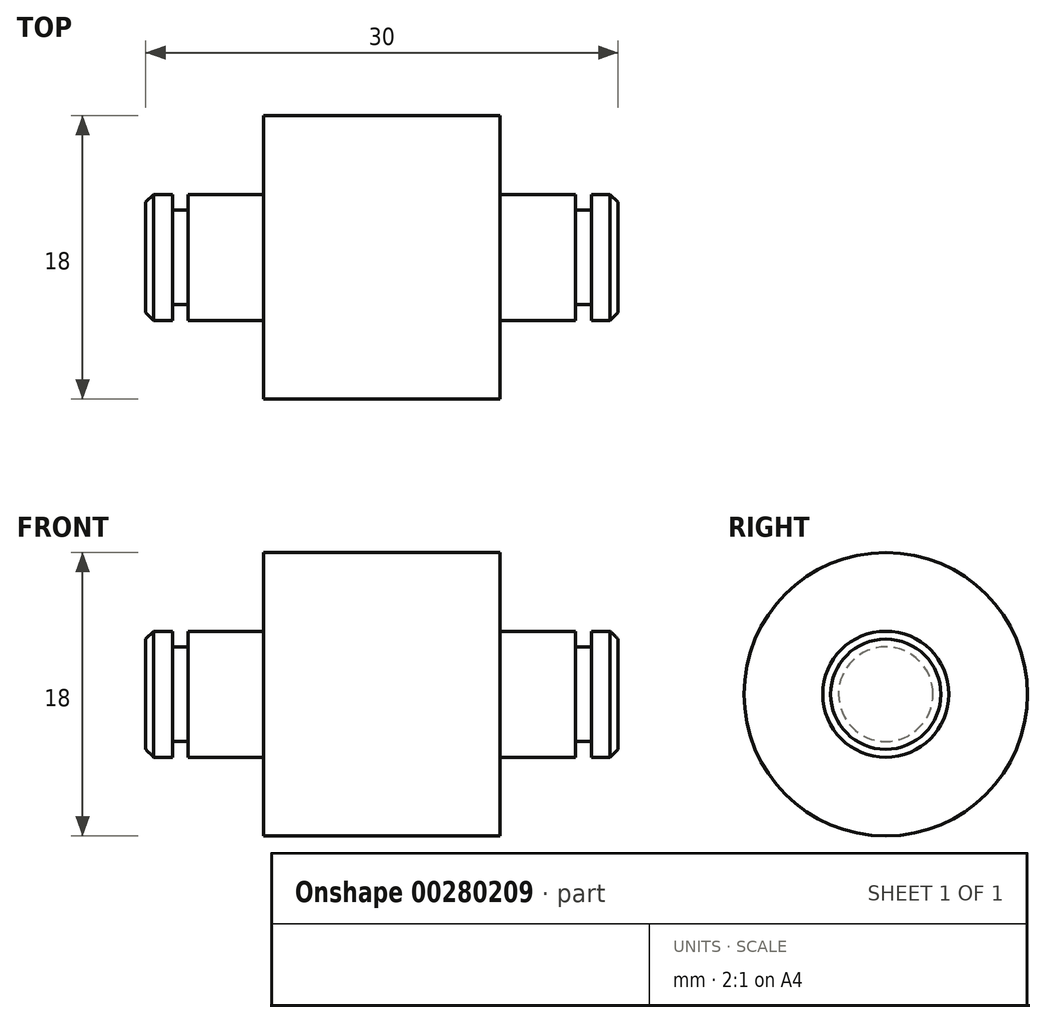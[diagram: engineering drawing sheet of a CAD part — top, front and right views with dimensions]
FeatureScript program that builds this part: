
annotation { "Feature Type Name" : "Feature", "Feature Type Description" : "" }
export const myFeature = defineFeature(function(context is Context, id is Id, definition is map)
    precondition{}
    {
        {
            var Q0;
            Q0=qCreatedBy(makeId("Front.planeOp"),FACE);
            var sketch = newSketch(context, id + "F0", { "sketchPlane" : qUnion([Q0])});
            skLineSegment(sketch, "E0", {"start": v(-15, 0) * mm, "end": v(-15, -4) * mm});
            skLineSegment(sketch, "E1", {"start": v(-15, -4) * mm, "end": v(-13.3, -4) * mm});
            skLineSegment(sketch, "E2", {"start": v(-13.3, -4) * mm, "end": v(-13.3, -3) * mm});
            skLineSegment(sketch, "E3", {"start": v(-7.5, -4) * mm, "end": v(-7.5, -9) * mm});
            skLineSegment(sketch, "E4", {"start": v(-7.5, -9) * mm, "end": v(7.5, -9) * mm});
            skLineSegment(sketch, "E5", {"start": v(7.5, -9) * mm, "end": v(7.5, -4) * mm});
            skLineSegment(sketch, "E6", {"start": v(13.3, -3) * mm, "end": v(13.3, -4) * mm});
            skLineSegment(sketch, "E7", {"start": v(13.3, -4) * mm, "end": v(15, -4) * mm});
            skLineSegment(sketch, "E8", {"start": v(15, -4) * mm, "end": v(15, 0) * mm});
            skLineSegment(sketch, "E9", {"start": v(15, 0) * mm, "end": v(-15, 0) * mm});
            skLineSegment(sketch, "E10", {"start": v(0, 0) * mm, "end": v(-24.48, 0) * mm, "construction": true});
            skLineSegment(sketch, "E11", {"start": v(-13.3, -3) * mm, "end": v(-12.3, -3) * mm});
            skLineSegment(sketch, "E12", {"start": v(-12.3, -3) * mm, "end": v(-12.3, -4) * mm});
            skLineSegment(sketch, "E13", {"start": v(-12.3, -4) * mm, "end": v(-7.5, -4) * mm});
            skLineSegment(sketch, "E14.MirrorCS", {"start": v(13.3, -3) * mm, "end": v(12.3, -3) * mm});
            skLineSegment(sketch, "E15.MirrorCS", {"start": v(12.3, -3) * mm, "end": v(12.3, -4) * mm});
            skLineSegment(sketch, "E16.MirrorCS", {"start": v(12.3, -4) * mm, "end": v(7.5, -4) * mm});
            skPoint(sketch, "E17.orphan", {"position": v(7.5, -4) * mm});
            skPoint(sketch, "E18.orphan", {"position": v(7.5, -3) * mm});
            skPoint(sketch, "E19.orphan", {"position": v(13.3, -3) * mm});
            skSolve(sketch);
        }
        {
            var Q0;
            Q0=makeQuery(id+"F0.imprint","IMPRINT",FACE,{"disambiguationData":[TD([[makeQuery(id+"F0.imprint","IMPRINT",EDGE,{"derivedFrom":sQuery(id+"F0.wireOp",EDGE,"E0")}),1.0]])]});
            var Q1;
            Q1=sQuery(id+"F0.wireOp",EDGE,"E10");
            revolve(context, id + "F1", {"entities" : qUnion([Q0]), "axis" : qUnion([Q1]), "revolveType" : RevolveType.FULL});
        }
        {
            var Q0;
            Q0=makeQuery(id+"F1.opRevolve","SWEPT_EDGE",EDGE,{"disambiguationData":[OSD([sQuery(id+"F0.wireOp",EDGE,"E7"),sQuery(id+"F0.wireOp",EDGE,"E8")])]});
            var Q1;
            Q1=makeQuery(id+"F1.opRevolve","SWEPT_EDGE",EDGE,{"disambiguationData":[OSD([sQuery(id+"F0.wireOp",EDGE,"E0"),sQuery(id+"F0.wireOp",EDGE,"E1")])]});
            chamfer(context, id + "F2", {"entities" : qUnion([Q0, Q1]), "chamferType" : ChamferType.OFFSET_ANGLE, "width" : .5 * mm, "oppositeDirection" : false, "angle" : 45 * degree, "tangentPropagation" : true});
        }
    });
